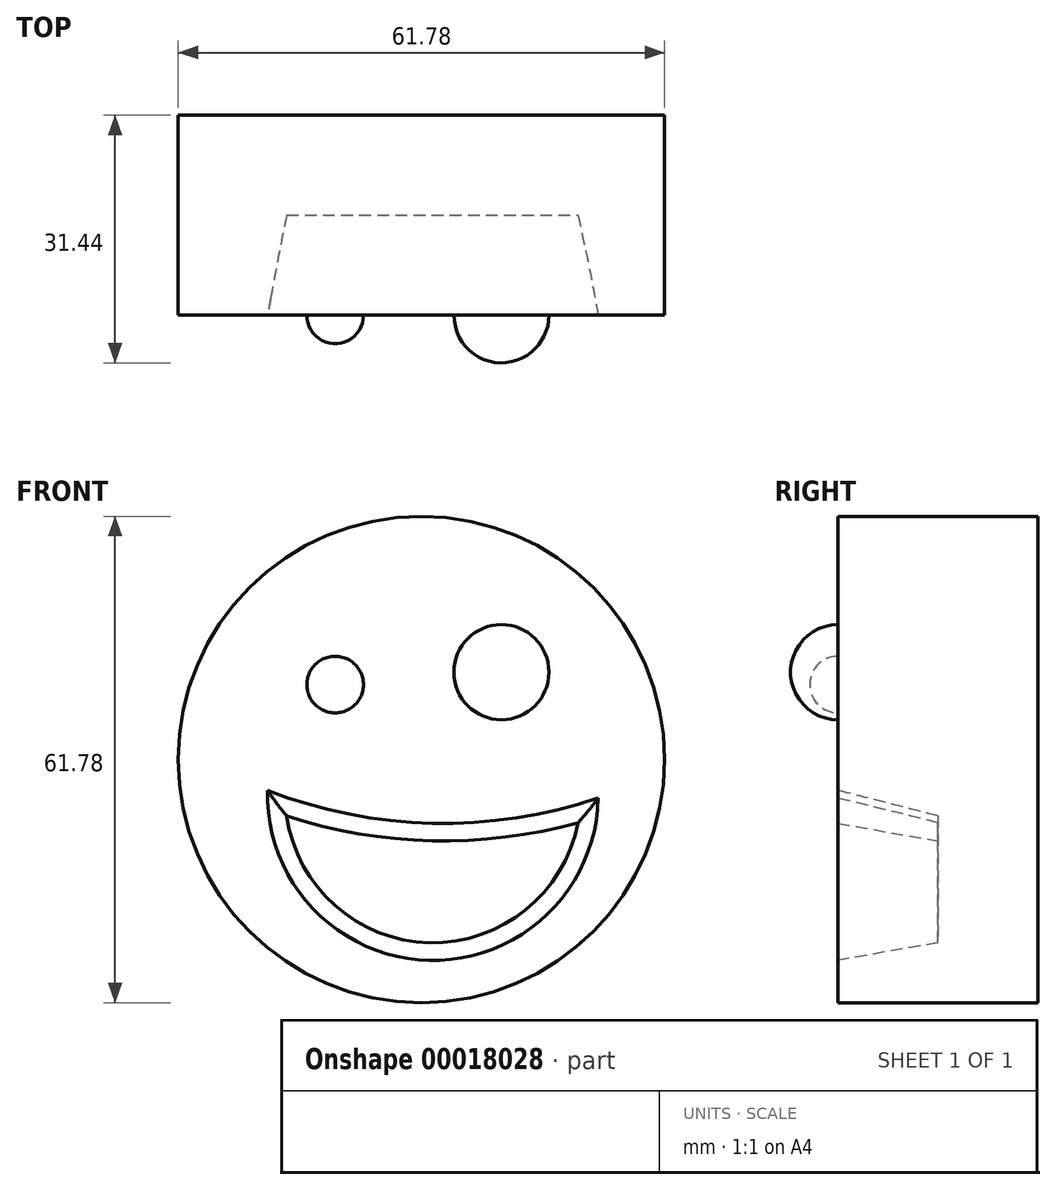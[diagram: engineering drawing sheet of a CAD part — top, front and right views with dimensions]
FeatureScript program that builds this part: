
annotation { "Feature Type Name" : "Feature", "Feature Type Description" : "" }
export const myFeature = defineFeature(function(context is Context, id is Id, definition is map)
    precondition{}
    {
        {
            var Q0;
            Q0=qCreatedBy(makeId("Front.planeOp"),FACE);
            var sketch = newSketch(context, id + "F0", { "sketchPlane" : qUnion([Q0])});
            skCircle(sketch, "E0", {"center": v(0, 0) * mm, "radius": 30.89 * mm});
            skSolve(sketch);
        }
        {
            var Q0;
            Q0 = qSketchRegion(id + "F0", true);
            extrude(context, id + "F1", {"entities" : qUnion([Q0]), "depth" : 25.4 * mm});
        }
        {
            var Q0;
            Q0=makeQuery(id+"F1.opExtrude","CAP_FACE",FACE,{"disambiguationData":[OSD([sQuery(id+"F0.wireOp",EDGE,"E0")])],"isStart":false});
            var sketch = newSketch(context, id + "F2", { "sketchPlane" : qUnion([Q0])});
            skLineSegment(sketch, "E1", {"start": v(-10.95, 13.11) * mm, "end": v(-10.95, 5.93) * mm});
            skArc(sketch, "E2", {"start": v(-10.95, 13.11) * mm, "mid": v(-14.55, 9.52) * mm, "end": v(-10.95, 5.93) * mm});
            skSolve(sketch);
        }
        {
            var Q0;
            Q0=makeQuery(id+"F2.imprint","IMPRINT",FACE,{"disambiguationData":[TD([[makeQuery(id+"F2.imprint","IMPRINT",EDGE,{"derivedFrom":sQuery(id+"F2.wireOp",EDGE,"E1")}),-1.0]])]});
            var Q1;
            Q1=sQuery(id+"F2.wireOp",EDGE,"E1");
            revolve(context, id + "F3", {"operationType" : NewBodyOperationType.ADD, "entities" : qUnion([Q0]), "axis" : qUnion([Q1]), "revolveType" : RevolveType.FULL});
        }
        {
            var Q0;
            Q0=makeQuery(id+"F1.opExtrude","CAP_FACE",FACE,{"disambiguationData":[OSD([sQuery(id+"F0.wireOp",EDGE,"E0")])],"isStart":false});
            var sketch = newSketch(context, id + "F4", { "sketchPlane" : qUnion([Q0])});
            skLineSegment(sketch, "E3", {"start": v(10.17, 17.14) * mm, "end": v(10.17, 5.05) * mm});
            skArc(sketch, "E4", {"start": v(10.17, 5.05) * mm, "mid": v(16.2, 11.1) * mm, "end": v(10.17, 17.14) * mm});
            skSolve(sketch);
        }
        {
            var Q0;
            Q0 = qSketchRegion(id + "F4", true);
            var Q1;
            Q1=sQuery(id+"F4.wireOp",EDGE,"E3");
            revolve(context, id + "F5", {"operationType" : NewBodyOperationType.ADD, "entities" : qUnion([Q0]), "axis" : qUnion([Q1]), "revolveType" : RevolveType.FULL});
        }
        {
            var Q0;
            Q0=makeQuery(id+"F1.opExtrude","CAP_FACE",FACE,{"disambiguationData":[OSD([sQuery(id+"F0.wireOp",EDGE,"E0")])],"isStart":false});
            var sketch = newSketch(context, id + "F6", { "sketchPlane" : qUnion([Q0])});
            skArc(sketch, "E5", {"start": v(-19.52, -3.94) * mm, "mid": v(1.38, -8.1) * mm, "end": v(22.45, -4.9) * mm});
            skArc(sketch, "E6", {"start": v(-19.52, -3.94) * mm, "mid": v(0.98, -25.5) * mm, "end": v(22.45, -4.9) * mm});
            skSolve(sketch);
        }
        {
            var Q0;
            Q0 = qSketchRegion(id + "F6", true);
            extrude(context, id + "F7", {"entities" : qUnion([Q0]), "operationType" : NewBodyOperationType.REMOVE, "oppositeDirection" : true, "depth" : 12.7 * mm, "hasDraft" : true, "draftAngle" : 10 * degree, "draftPullDirection" : true});
        }
    });
